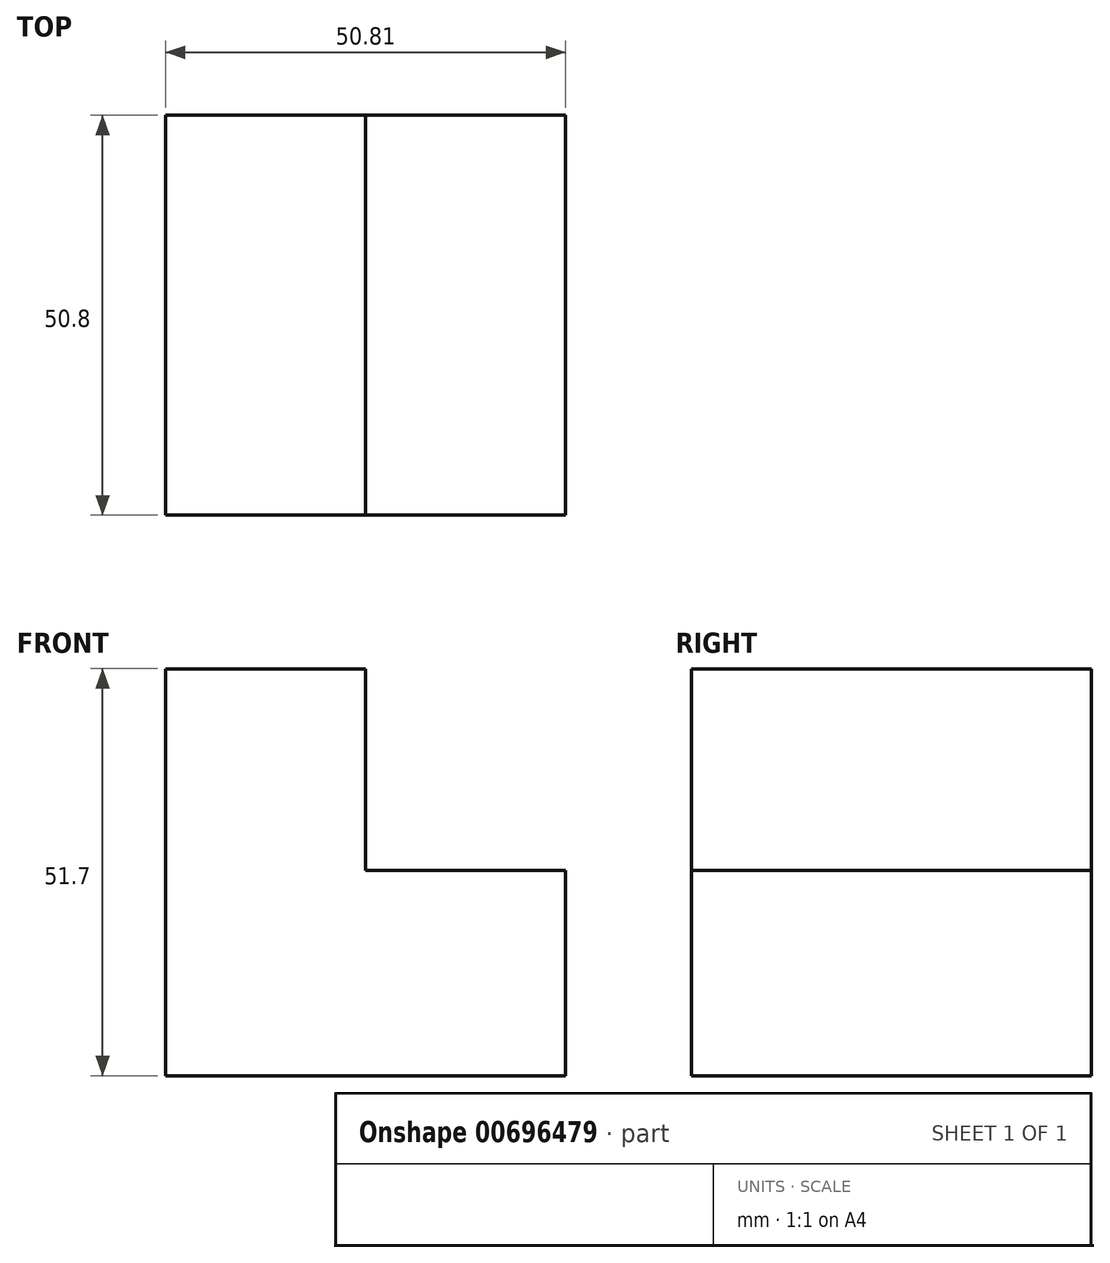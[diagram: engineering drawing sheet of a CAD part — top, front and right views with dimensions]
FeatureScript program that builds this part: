
annotation { "Feature Type Name" : "Feature", "Feature Type Description" : "" }
export const myFeature = defineFeature(function(context is Context, id is Id, definition is map)
    precondition{}
    {
        {
            var Q0;
            Q0=qCreatedBy(makeId("Front.planeOp"),FACE);
            var sketch = newSketch(context, id + "F0", { "sketchPlane" : qUnion([Q0])});
            skLineSegment(sketch, "E0", {"start": v(0, 0) * mm, "end": v(0, 51.7) * mm});
            skLineSegment(sketch, "E1", {"start": v(0, 51.7) * mm, "end": v(25.38, 51.7) * mm});
            skLineSegment(sketch, "E2", {"start": v(25.38, 51.7) * mm, "end": v(25.38, 26.05) * mm});
            skLineSegment(sketch, "E3", {"start": v(25.38, 26.05) * mm, "end": v(50.8, 26.05) * mm});
            skLineSegment(sketch, "E4", {"start": v(50.8, 26.05) * mm, "end": v(50.8, 0) * mm});
            skLineSegment(sketch, "E5", {"start": v(50.8, 0) * mm, "end": v(0, 0) * mm});
            skSolve(sketch);
        }
        {
            var Q0;
            Q0 = qSketchRegion(id + "F0", true);
            extrude(context, id + "F1", {"entities" : qUnion([Q0]), "depth" : 50.8 * mm, "offsetDistance" : 25.4 * mm});
        }
    });
